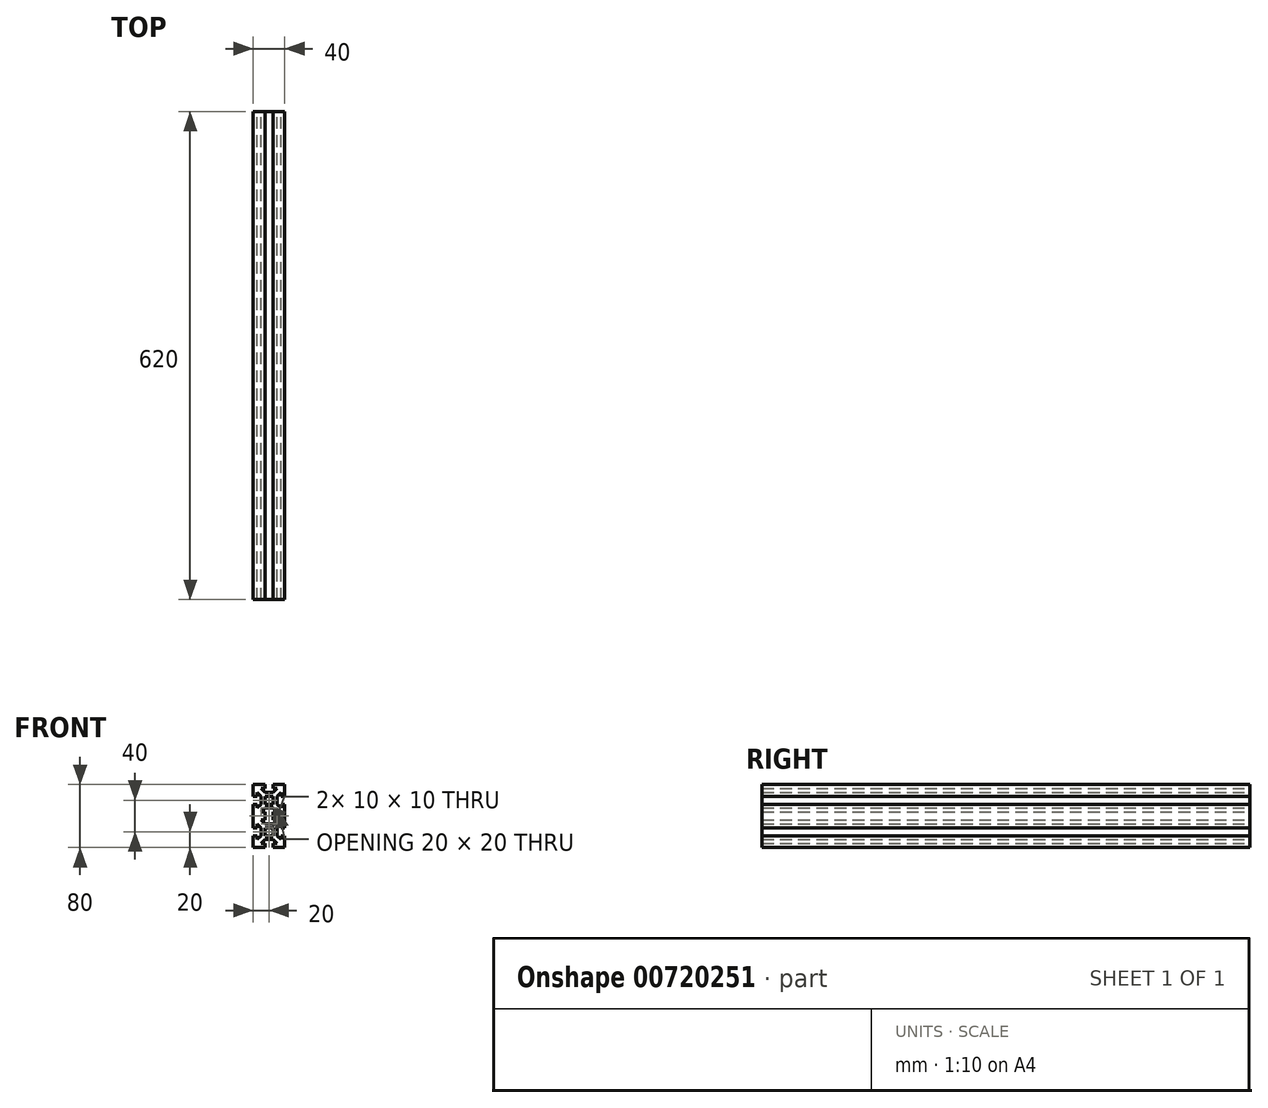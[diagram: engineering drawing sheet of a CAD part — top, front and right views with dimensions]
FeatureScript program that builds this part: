
annotation { "Feature Type Name" : "Feature", "Feature Type Description" : "" }
export const myFeature = defineFeature(function(context is Context, id is Id, definition is map)
    precondition{}
    {
        {
            var Q0;
            Q0=qCreatedBy(makeId("Front.planeOp"),FACE);
            var sketch = newSketch(context, id + "F0", { "sketchPlane" : qUnion([Q0])});
            skLineSegment(sketch, "E0.top", {"start": v(20, -20) * mm, "end": v(5, -20) * mm});
            skLineSegment(sketch, "E0.left", {"start": v(20, 20) * mm, "end": v(20, 5) * mm});
            skLineSegment(sketch, "E0.right", {"start": v(-20, 20) * mm, "end": v(-20, 5) * mm});
            skPoint(sketch, "E0.middle", {"position": v(0, 0) * mm});
            skLineSegment(sketch, "E1", {"start": v(0, 20) * mm, "end": v(0, -20) * mm, "construction": true});
            skLineSegment(sketch, "E2", {"start": v(-20, 0) * mm, "end": v(20, 0) * mm, "construction": true});
            skLineSegment(sketch, "E3", {"start": v(-20, 5) * mm, "end": v(-15, 5) * mm});
            skLineSegment(sketch, "E4", {"start": v(-20, -5) * mm, "end": v(-15, -5) * mm});
            skLineSegment(sketch, "E5", {"start": v(-5, 20) * mm, "end": v(-5, 15) * mm});
            skLineSegment(sketch, "E6", {"start": v(5, 20) * mm, "end": v(5, 15) * mm});
            skLineSegment(sketch, "E7", {"start": v(-10, 15) * mm, "end": v(-5, 15) * mm});
            skLineSegment(sketch, "E8", {"start": v(-10, -15) * mm, "end": v(-5, -15) * mm});
            skLineSegment(sketch, "E9", {"start": v(15, 10) * mm, "end": v(15, 5) * mm});
            skLineSegment(sketch, "E10", {"start": v(-15, 10) * mm, "end": v(-10, 5) * mm});
            skLineSegment(sketch, "E11", {"start": v(-10, 15) * mm, "end": v(-5, 10) * mm});
            skLineSegment(sketch, "E12", {"start": v(-15, -10) * mm, "end": v(-10, -5) * mm});
            skLineSegment(sketch, "E13", {"start": v(-10, -15) * mm, "end": v(-5, -10) * mm});
            skLineSegment(sketch, "E14.trimOffspring", {"start": v(20, -5) * mm, "end": v(20, -20) * mm});
            skLineSegment(sketch, "E15.trimOffspring", {"start": v(-20, -5) * mm, "end": v(-20, -20) * mm});
            skLineSegment(sketch, "E16.trimOffspring", {"start": v(-5, -20) * mm, "end": v(-20, -20) * mm});
            skLineSegment(sketch, "E17.trimOffspring", {"start": v(5, 15) * mm, "end": v(10, 15) * mm});
            skLineSegment(sketch, "E18.trimOffspring", {"start": v(-15, -5) * mm, "end": v(-15, -10) * mm});
            skLineSegment(sketch, "E19.trimOffspring", {"start": v(15, -5) * mm, "end": v(15, -10) * mm});
            skLineSegment(sketch, "E20.trimOffspring", {"start": v(5, -15) * mm, "end": v(10, -15) * mm});
            skLineSegment(sketch, "E21.trimOffspring", {"start": v(-5, 5) * mm, "end": v(-5, -5) * mm});
            skLineSegment(sketch, "E22.trimOffspring", {"start": v(5, 5) * mm, "end": v(5, -5) * mm});
            skLineSegment(sketch, "E23.trimOffspring", {"start": v(15, 5) * mm, "end": v(20, 5) * mm});
            skLineSegment(sketch, "E24.trimOffspring", {"start": v(15, -5) * mm, "end": v(20, -5) * mm});
            skLineSegment(sketch, "E25.trimOffspring", {"start": v(5, -15) * mm, "end": v(5, -20) * mm});
            skLineSegment(sketch, "E26.trimOffspring", {"start": v(-5, -15) * mm, "end": v(-5, -20) * mm});
            skLineSegment(sketch, "E27.trimOffspring", {"start": v(-5, -5) * mm, "end": v(5, -5) * mm});
            skLineSegment(sketch, "E28.trimOffspring", {"start": v(-5, 5) * mm, "end": v(5, 5) * mm});
            skLineSegment(sketch, "E29", {"start": v(10, 5) * mm, "end": v(10, -5) * mm});
            skLineSegment(sketch, "E30", {"start": v(-5, 10) * mm, "end": v(5, 10) * mm});
            skLineSegment(sketch, "E31", {"start": v(-10, 5) * mm, "end": v(-10, -5) * mm});
            skLineSegment(sketch, "E32", {"start": v(-5, -10) * mm, "end": v(5, -10) * mm});
            skLineSegment(sketch, "E33.trimOffspring", {"start": v(-15, 10) * mm, "end": v(-15, 5) * mm});
            skPoint(sketch, "E34.orphan", {"position": v(20, 15) * mm});
            skPoint(sketch, "E35.orphan", {"position": v(20, -15) * mm});
            skPoint(sketch, "E36.orphan", {"position": v(15, -20) * mm});
            skPoint(sketch, "E37.orphan", {"position": v(-15, -20) * mm});
            skLineSegment(sketch, "E38.trimOffspring", {"start": v(-5, 0) * mm, "end": v(0, -5) * mm});
            skLineSegment(sketch, "E39.trimOffspring", {"start": v(-5, 0) * mm, "end": v(0, 5) * mm});
            skLineSegment(sketch, "E40.trimOffspring", {"start": v(0, 5) * mm, "end": v(5, 0) * mm});
            skLineSegment(sketch, "E41.trimOffspring", {"start": v(5, 10) * mm, "end": v(10, 15) * mm});
            skLineSegment(sketch, "E42.trimOffspring", {"start": v(10, 5) * mm, "end": v(15, 10) * mm});
            skLineSegment(sketch, "E43.trimOffspring", {"start": v(10, -5) * mm, "end": v(15, -10) * mm});
            skLineSegment(sketch, "E44.trimOffspring", {"start": v(5, -10) * mm, "end": v(10, -15) * mm});
            skLineSegment(sketch, "E45.trimOffspring", {"start": v(0, -5) * mm, "end": v(5, 0) * mm});
            skLineSegment(sketch, "E46.bottom", {"start": v(20, 60) * mm, "end": v(5, 60) * mm});
            skLineSegment(sketch, "E46.left", {"start": v(20, 60) * mm, "end": v(20, 45) * mm});
            skLineSegment(sketch, "E46.right", {"start": v(-20, 60) * mm, "end": v(-20, 45) * mm});
            skPoint(sketch, "E46.middle", {"position": v(0, 40) * mm});
            skLineSegment(sketch, "E47", {"start": v(0, 60) * mm, "end": v(0, 20) * mm, "construction": true});
            skLineSegment(sketch, "E48", {"start": v(-20, 40) * mm, "end": v(20, 40) * mm, "construction": true});
            skLineSegment(sketch, "E49", {"start": v(-20, 45) * mm, "end": v(-15, 45) * mm});
            skLineSegment(sketch, "E50", {"start": v(-20, 35) * mm, "end": v(-15, 35) * mm});
            skLineSegment(sketch, "E51", {"start": v(-5, 60) * mm, "end": v(-5, 55) * mm});
            skLineSegment(sketch, "E52", {"start": v(5, 60) * mm, "end": v(5, 55) * mm});
            skLineSegment(sketch, "E53", {"start": v(-10, 55) * mm, "end": v(-5, 55) * mm});
            skLineSegment(sketch, "E54", {"start": v(-10, 25) * mm, "end": v(-5, 25) * mm});
            skLineSegment(sketch, "E55", {"start": v(15, 50) * mm, "end": v(15, 45) * mm});
            skLineSegment(sketch, "E56", {"start": v(-15, 50) * mm, "end": v(-10, 45) * mm});
            skLineSegment(sketch, "E57", {"start": v(-10, 55) * mm, "end": v(-5, 50) * mm});
            skLineSegment(sketch, "E58", {"start": v(-15, 30) * mm, "end": v(-10, 35) * mm});
            skLineSegment(sketch, "E59", {"start": v(-10, 25) * mm, "end": v(-5, 30) * mm});
            skLineSegment(sketch, "E60.trimOffspring", {"start": v(20, 35) * mm, "end": v(20, 20) * mm});
            skLineSegment(sketch, "E61.trimOffspring", {"start": v(-20, 35) * mm, "end": v(-20, 20) * mm});
            skLineSegment(sketch, "E62.trimOffspring", {"start": v(-5, 60) * mm, "end": v(-20, 60) * mm});
            skLineSegment(sketch, "E63.trimOffspring", {"start": v(5, 55) * mm, "end": v(10, 55) * mm});
            skLineSegment(sketch, "E64.trimOffspring", {"start": v(-15, 35) * mm, "end": v(-15, 30) * mm});
            skLineSegment(sketch, "E65.trimOffspring", {"start": v(15, 35) * mm, "end": v(15, 30) * mm});
            skLineSegment(sketch, "E66.trimOffspring", {"start": v(5, 25) * mm, "end": v(10, 25) * mm});
            skLineSegment(sketch, "E67.trimOffspring", {"start": v(-5, 45) * mm, "end": v(-5, 35) * mm});
            skLineSegment(sketch, "E68.trimOffspring", {"start": v(5, 45) * mm, "end": v(5, 35) * mm});
            skLineSegment(sketch, "E69.trimOffspring", {"start": v(15, 45) * mm, "end": v(20, 45) * mm});
            skLineSegment(sketch, "E70.trimOffspring", {"start": v(15, 35) * mm, "end": v(20, 35) * mm});
            skLineSegment(sketch, "E71.trimOffspring", {"start": v(5, 25) * mm, "end": v(5, 20) * mm});
            skLineSegment(sketch, "E72.trimOffspring", {"start": v(-5, 25) * mm, "end": v(-5, 20) * mm});
            skLineSegment(sketch, "E73.trimOffspring", {"start": v(-5, 35) * mm, "end": v(5, 35) * mm});
            skLineSegment(sketch, "E74.trimOffspring", {"start": v(-5, 45) * mm, "end": v(5, 45) * mm});
            skLineSegment(sketch, "E75", {"start": v(10, 45) * mm, "end": v(10, 35) * mm});
            skLineSegment(sketch, "E76", {"start": v(-5, 50) * mm, "end": v(5, 50) * mm});
            skLineSegment(sketch, "E77", {"start": v(-10, 45) * mm, "end": v(-10, 35) * mm});
            skLineSegment(sketch, "E78", {"start": v(-5, 30) * mm, "end": v(5, 30) * mm});
            skLineSegment(sketch, "E79.trimOffspring", {"start": v(-15, 50) * mm, "end": v(-15, 45) * mm});
            skPoint(sketch, "E80.orphan", {"position": v(20, 55) * mm});
            skPoint(sketch, "E81.orphan", {"position": v(20, 25) * mm});
            skPoint(sketch, "E82.orphan", {"position": v(15, 20) * mm});
            skLineSegment(sketch, "E83.trimOffspring", {"start": v(-5, 40) * mm, "end": v(0, 35) * mm});
            skLineSegment(sketch, "E84.trimOffspring", {"start": v(-5, 40) * mm, "end": v(0, 45) * mm});
            skLineSegment(sketch, "E85.trimOffspring", {"start": v(0, 45) * mm, "end": v(5, 40) * mm});
            skLineSegment(sketch, "E86.trimOffspring", {"start": v(5, 50) * mm, "end": v(10, 55) * mm});
            skLineSegment(sketch, "E87.trimOffspring", {"start": v(10, 45) * mm, "end": v(15, 50) * mm});
            skLineSegment(sketch, "E88.trimOffspring", {"start": v(10, 35) * mm, "end": v(15, 30) * mm});
            skLineSegment(sketch, "E89.trimOffspring", {"start": v(5, 30) * mm, "end": v(10, 25) * mm});
            skLineSegment(sketch, "E90.trimOffspring", {"start": v(0, 35) * mm, "end": v(5, 40) * mm});
            skSolve(sketch);
        }
        {
            var Q0;
            Q0=makeQuery(id+"F0.imprint","IMPRINT",FACE,{"disambiguationData":[TD([[makeQuery(id+"F0.imprint","IMPRINT",EDGE,{"derivedFrom":sQuery(id+"F0.wireOp",EDGE,"E0.top")}),-1.0]])]});
            extrude(context, id + "F1", {"entities" : qUnion([Q0]), "depth" : 620 * mm, "offsetDistance" : 25 * mm});
        }
    });
